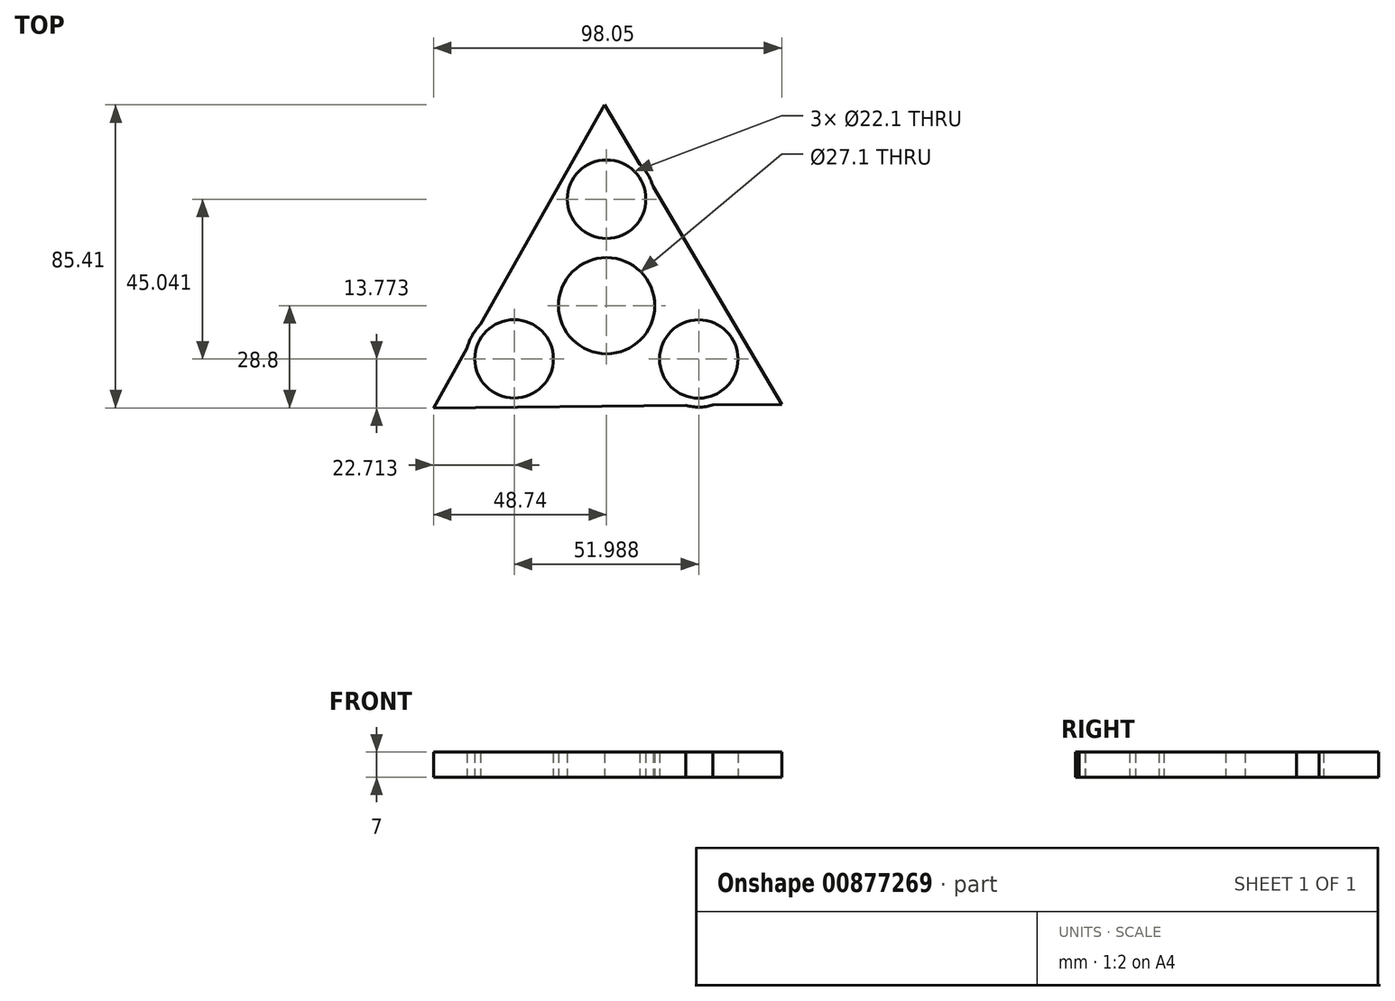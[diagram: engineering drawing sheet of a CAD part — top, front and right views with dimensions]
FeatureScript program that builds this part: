
annotation { "Feature Type Name" : "Feature", "Feature Type Description" : "" }
export const myFeature = defineFeature(function(context is Context, id is Id, definition is map)
    precondition{}
    {
        {
            var Q0;
            Q0=qCreatedBy(makeId("Top.planeOp"),FACE);
            var sketch = newSketch(context, id + "F0", { "sketchPlane" : qUnion([Q0])});
            skCircle(sketch, "E0", {"center": v(0, 0) * mm, "radius": 11.05 * mm});
            skCircle(sketch, "E1", {"center": v(0, 0) * mm, "radius": 13.55 * mm});
            skCircle(sketch, "E2", {"center": v(0, 30.01) * mm, "radius": 11.05 * mm});
            skCircle(sketch, "E3", {"center": v(0, 30.01) * mm, "radius": 13.55 * mm});
            skCircle(sketch, "E4.1.0", {"center": v(-26.03, -14.99) * mm, "radius": 11.05 * mm});
            skCircle(sketch, "E4.1.1", {"center": v(-26.03, -14.99) * mm, "radius": 13.55 * mm});
            skCircle(sketch, "E4.2.0", {"center": v(25.96, -15.03) * mm, "radius": 11.05 * mm});
            skCircle(sketch, "E4.2.1", {"center": v(25.96, -15.03) * mm, "radius": 13.55 * mm});
            skPoint(sketch, "E4.center", {"position": v(-0.02, 0) * mm});
            skCircle(sketch, "E5.cCircle", {"center": v(0, 0) * mm, "radius": 56.6 * mm, "construction": true});
            skLineSegment(sketch, "E5.0", {"start": v(-48.74, -28.8) * mm, "end": v(-0.58, 56.6) * mm});
            skLineSegment(sketch, "E5.1", {"start": v(-0.58, 56.6) * mm, "end": v(49.31, -27.8) * mm});
            skLineSegment(sketch, "E5.2", {"start": v(49.31, -27.8) * mm, "end": v(-48.74, -28.8) * mm});
            skSolve(sketch);
        }
        {
            var Q0;
            Q0 = qSketchRegion(id + "F0", true);
            extrude(context, id + "F1", {"entities" : qUnion([Q0]), "depth" : 7 * mm, "offsetDistance" : 25 * mm});
        }
    });
